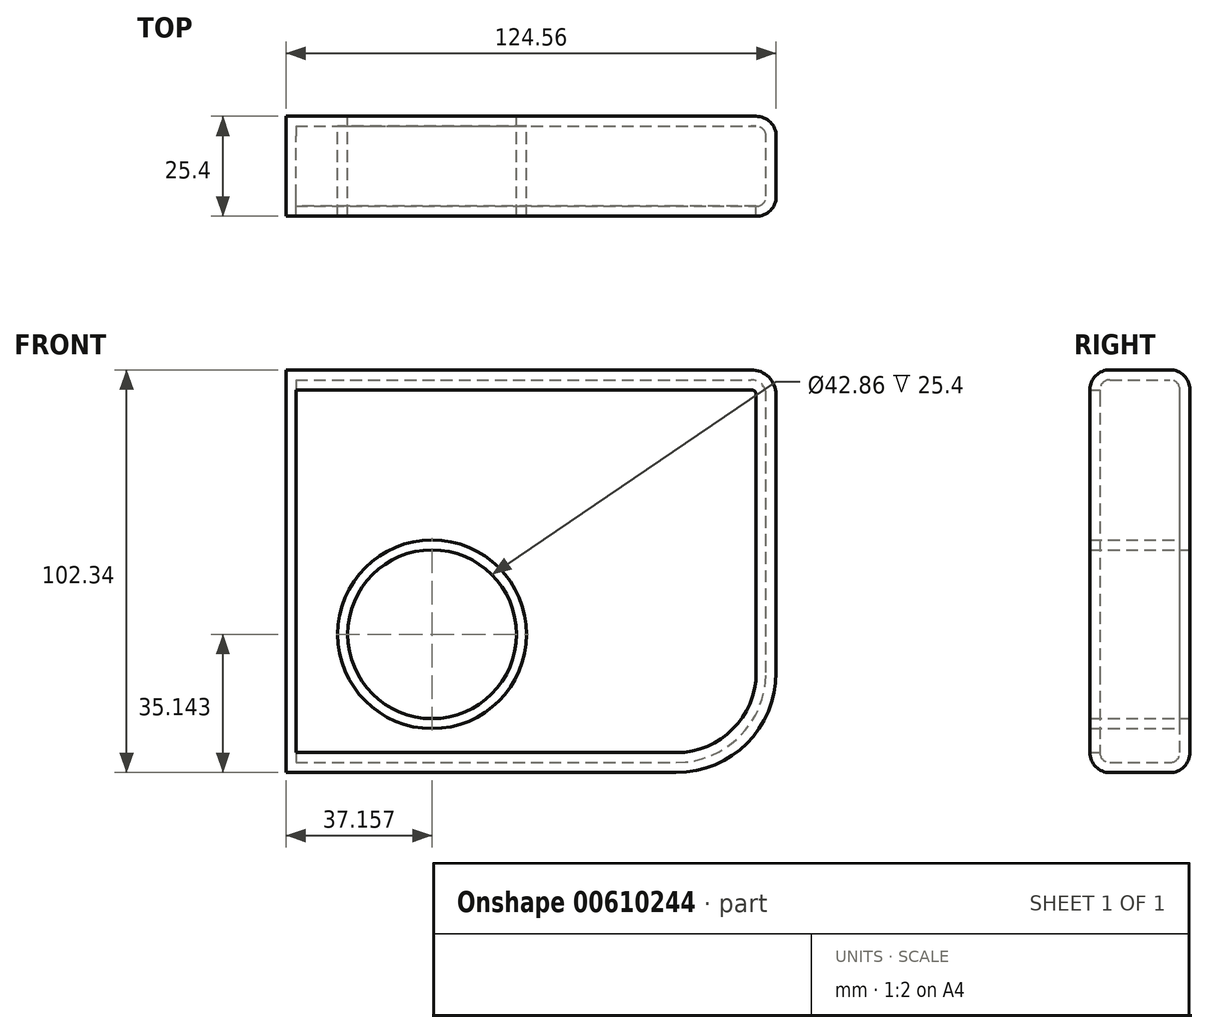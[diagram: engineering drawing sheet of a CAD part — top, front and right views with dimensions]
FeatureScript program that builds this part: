
annotation { "Feature Type Name" : "Feature", "Feature Type Description" : "" }
export const myFeature = defineFeature(function(context is Context, id is Id, definition is map)
    precondition{}
    {
        {
            var Q0;
            Q0=qCreatedBy(makeId("Front.planeOp"),FACE);
            var sketch = newSketch(context, id + "F0", { "sketchPlane" : qUnion([Q0])});
            skLineSegment(sketch, "E0.bottom", {"start": v(0, 0) * mm, "end": v(99.16, 0) * mm});
            skLineSegment(sketch, "E0.top", {"start": v(0, 102.34) * mm, "end": v(118.2, 102.34) * mm});
            skLineSegment(sketch, "E0.left", {"start": v(0, 0) * mm, "end": v(0, 102.34) * mm});
            skLineSegment(sketch, "E0.right", {"start": v(124.56, 25.4) * mm, "end": v(124.56, 95.99) * mm});
            skCircle(sketch, "E1", {"center": v(37.16, 35.14) * mm, "radius": 21.43 * mm});
            skPoint(sketch, "E2.visualSharp", {"position": v(124.56, 102.34) * mm});
            skArc(sketch, "E2.filletArc", {"start": v(124.56, 95.99) * mm, "mid": v(122.7, 100.48) * mm, "end": v(118.2, 102.34) * mm});
            skPoint(sketch, "E3.visualSharp", {"position": v(124.56, 0) * mm});
            skArc(sketch, "E3.filletArc", {"start": v(99.16, 0) * mm, "mid": v(117.12, 7.44) * mm, "end": v(124.56, 25.4) * mm});
            skSolve(sketch);
        }
        {
            var Q0;
            Q0 = qSketchRegion(id + "F0", true);
            extrude(context, id + "F1", {"entities" : qUnion([Q0]), "endBound" : BoundingType.SYMMETRIC, "depth" : 25.4 * mm, "offsetDistance" : 25.4 * mm});
        }
        {
            var Q0;
            Q0=makeQuery(id+"F1.opExtrude","CAP_EDGE",EDGE,{"disambiguationData":[OSD([sQuery(id+"F0.wireOp",EDGE,"E0.top")])],"isStart":true});
            var Q1;
            Q1=makeQuery(id+"F1.opExtrude","CAP_EDGE",EDGE,{"disambiguationData":[OSD([sQuery(id+"F0.wireOp",EDGE,"E0.top")])],"isStart":false});
            fillet(context, id + "F2", {"entities" : qUnion([Q0, Q1]), "radius" : 5.08 * mm, "tangentPropagation" : true, "allowEdgeOverflow" : false});
        }
        {
            var Q0;
            Q0=makeQuery(id+"F1.opExtrude","CAP_FACE",FACE,{"disambiguationData":[OSD([sQuery(id+"F0.wireOp",EDGE,"E0.bottom"),sQuery(id+"F0.wireOp",EDGE,"E0.top"),sQuery(id+"F0.wireOp",EDGE,"E0.left"),sQuery(id+"F0.wireOp",EDGE,"E0.right"),sQuery(id+"F0.wireOp",EDGE,"E1"),sQuery(id+"F0.wireOp",EDGE,"E2.filletArc"),sQuery(id+"F0.wireOp",EDGE,"E3.filletArc")])],"isStart":false});
            shell(context, id + "F3", {"entities" : qUnion([Q0]), "thickness" : 2.54 * mm});
        }
    });
